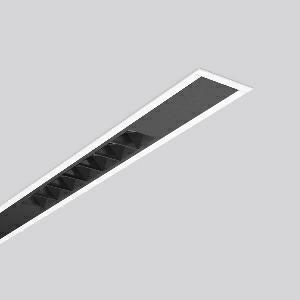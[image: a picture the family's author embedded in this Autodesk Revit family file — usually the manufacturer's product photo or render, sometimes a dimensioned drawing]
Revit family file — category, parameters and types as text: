
# Revit family: less_is_more_beamline_312469_002_dad4
name_source: partatom
category: Lighting Fixtures
units: mm (PartAtom-declared; Revit-internal decimal feet)

## family parameters
Cut with Voids When Loaded = No
Host = Face
Light Source = No
Part Type = Normal
Room Calculation Point = No
Round Connector Dimension = Use Diameter
Shared = No

## types (1)
- LESS IS MORE BEAMLINE (1 x LED Modul 930, 1750 lm, 3000)
    Apparent Load = 48 VA
    CIE Flux Codes = 100 100 100 100 100
    Color Rendering = 90
    Color Temperature = 3000
    Default Elevation = 1800 mm
    Description = Series: LESS IS MORE BEAMLINE
Linear recessed ceiling and wall luminaire for aesthetically sophisticated lighting. Luminaire with two LED light units. Housing: extruded aluminium profile, powder-coated. End cap aluminium powder-coated. LED light unit with MRS technology: Mini-Reflector-System made of metallised thermoplastic with prismatic black glare-suppressing frame for pleasant glare-free light (RUG < 10). Each LED light unit has 7 reflector elements. Medium beam light distribution. Ceiling installation with pre-assembled SBS mounting system. LED unit with integrated converter interchangeable and removable. Suitable for through-wiring. 
Colour: traffic white, matt (RAL 9016)
Length: 1141 mm
Width: 71 mm
Height: 1.5 mm
Cut-out length: 1128 mm
Cut-out width: 60 mm
Recess height: 125 mm
Luminaire: recess height: 106 mm
Lamp: LED
Socket: without socket
Colour temperature: 3000K
Colour rendering index (CRI): 90
System power: 48 W
Rated luminous flux: 3500 lm
Luminous efficiency: 73 lm/W
Control gear: Regulated power supply
Protection class: I
Type of protection: IP 20
    Height = 0 mm  [stored 0 ft]
    Lamp = 1 x LED Modul 930
    Lamp Light Flux = 1750 lm
    Lamp count = 1
    Length = 1141 mm
    Lifetime = 50000 h
    Luminous efficacy = 73 lm/W
    Manufacturer = RZB
    ModVariant = No
    Model = 312469.002
    Mounting Place = Ceiling, Wall
    Mounting Type = Recessed
    Number of Poles = 1
    OnlyDefault = Yes
    Power Factor = 1
    Product Name = LESS IS MORE BEAMLINE
    Product group = Recessed LED linear luminaires
    ProductGroupID = 407
    Protection Class = Protection class I
    Protection Degree = IP 20
    RLX_Detail_Level = 1
    RLX_Emergency_Light_Flux = 0 lm
    RLX_Emergency_Type = 0
    RLX_Emergency_Type_DB = No
    RlxData = <blob elided: 23685 chars, md5=8de3cde0>
    Socket = socket
    Standby Power = 0 W
    System Light Flux = 3500 lm
    System Power = 48 W
    Type Comments = Product without accessories
    Type Image = 312465.002.jpg
    URL = http://relux.com
    VarID = ---
    Voltage = 230 V
    Voltage Range = 220-240 V
    Weight = 0.00 kg
    Width = 71 mm

note: [stored X ft] marks values corroborated as IEEE doubles in the binary element streams (Revit-internal decimal feet)

## geometry (parser evidence)
native form markers: Blend x4, Sweep x14
no freeform markers — native parametric forms only
